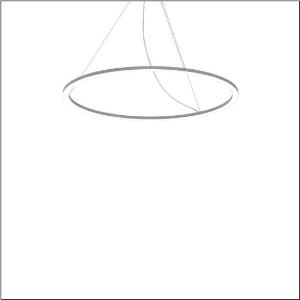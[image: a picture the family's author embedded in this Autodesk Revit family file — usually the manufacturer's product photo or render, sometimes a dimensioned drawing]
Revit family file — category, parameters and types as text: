
# Revit family: silica_r__21_ring-d_5pjbd3d3204a_b808
name_source: partatom
category: Lighting Fixtures
units: mm (PartAtom-declared; Revit-internal decimal feet)

## family parameters
Cut with Voids When Loaded = No
Host = Face
Light Source = No
Part Type = Normal
Room Calculation Point = No
Round Connector Dimension = Use Diameter
Shared = No

## types (1)
- Silica® 21 Ring-D (1 x LED, 8420 lm, 94 W, 4000K)
    Apparent Load = 94 VA
    CIE Flux Codes = 37 69 92 100 100
    Color Rendering = 80
    Color Temperature = 4000K
    Default Elevation = 1800 mm
    Description = Silica® 21 Ring-D, suspended luminaire, of PMMA, frosted, light emission: ring underside luminous distribution, primary light characteristic: symmetric, installation type: suspended mounting, LED, rated luminous flux: 8.420lm, luminous efficacy: 90lm/W, light colour: 840, colour temperature: 4000K, with terminal, 5-pole, mains connection: 230V, AC/DC, 0/50..60Hz, rated input power: 94W, housing, of extruded aluminium section, metallic grey (RAL 9006), diameter: 1.100mm, ceiling canopy, metallic grey (RAL 9006), protection rating (lamp compartment): IP40, insulation class (complete): insulation class I (protective earthing), certification: CE, impact resistance: IK02, permissible operating ambient temperature: 0..+35°C, packaging unit: 1 piece
    Height = 25 mm  [stored 0.082021 ft]
    Lamp = 1 x LED
    Lamp Light Flux = 8420 lm
    Lamp Power = 94 W
    Lamp count = 1
    Length = 1100 mm
    Luminous efficacy = 90 lm/W
    Manufacturer = Siteco
    ModVariant = No
    Model = 5PJBD3D3204A
    Mounting Place = Ceiling
    Mounting Type = Pendant
    Number of Poles = 1
    OnlyDefault = Yes
    Power Factor = 1
    Product Name = Silica® 21 Ring-D
    Product group = suspended luminaire
    ProductGroupID = 904
    Protection Class = Protection class I
    Protection Degree = Degree of protection
    RLX_Detail_Level = 1
    RLX_Emergency_Light_Flux = 0 lm
    RLX_Emergency_Type = 0
    RLX_Emergency_Type_DB = No
    RlxData = <blob elided: 14549 chars, md5=448e10b4>
    Socket = socket
    Standby Power = 0 W
    System Light Flux = 8420 lm
    System Power = 94 W
    Type Comments = Product without accessories
    Type Image = l_1251746.jpg
    URL = http://relux.com
    VarID = ---
    Voltage = 0 V
    Weight = 0.00 kg
    Width = 0 mm  [stored 0 ft]

note: [stored X ft] marks values corroborated as IEEE doubles in the binary element streams (Revit-internal decimal feet)

## geometry (parser evidence)
native form markers: Sweep x12
no freeform markers — native parametric forms only
